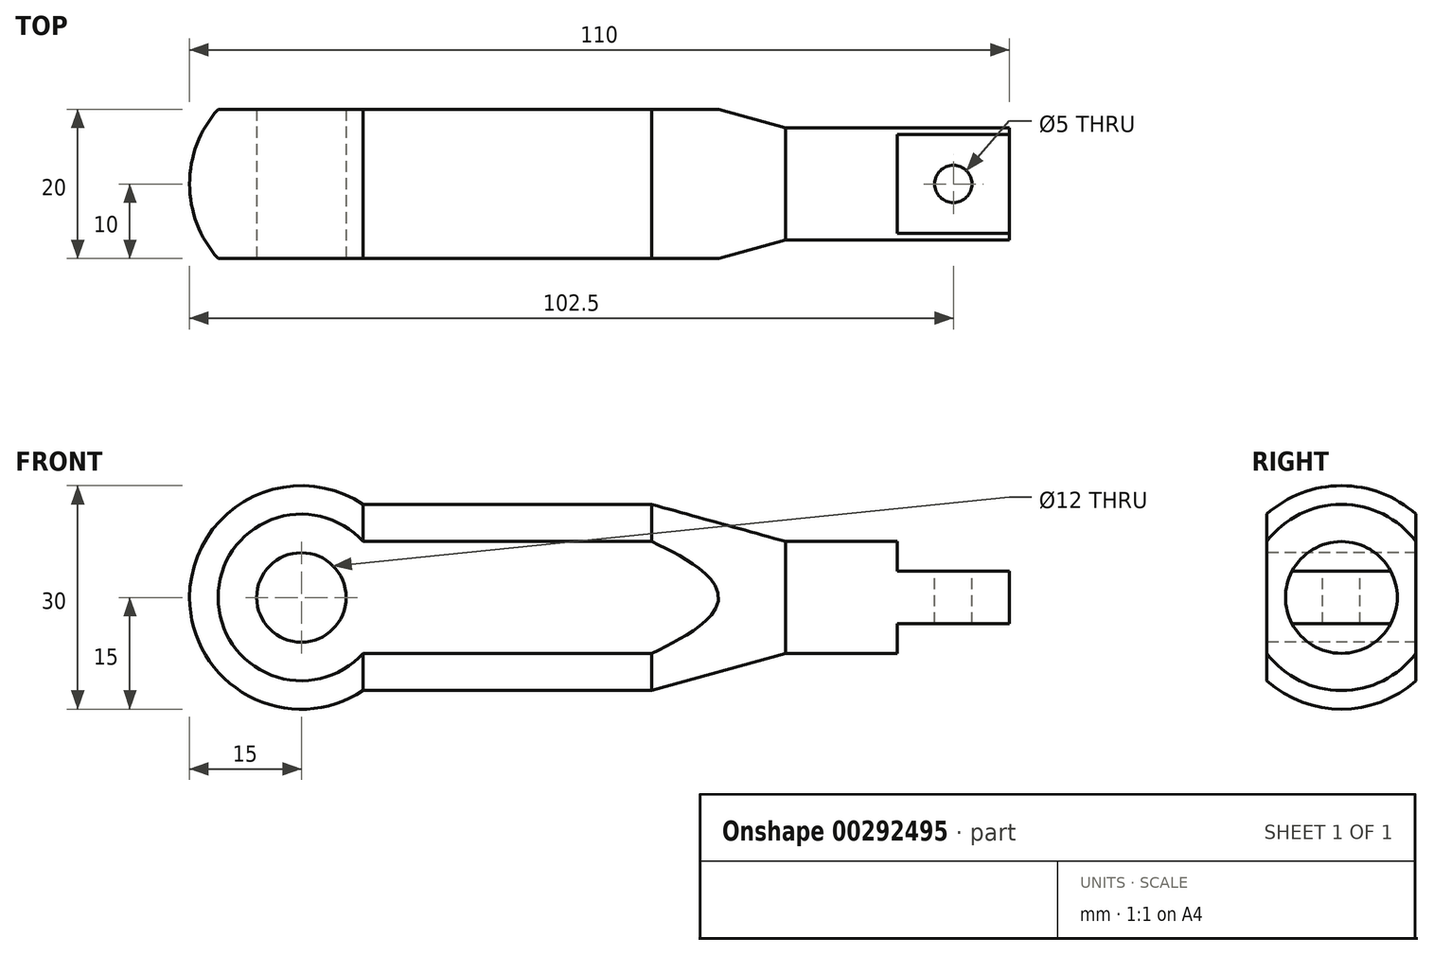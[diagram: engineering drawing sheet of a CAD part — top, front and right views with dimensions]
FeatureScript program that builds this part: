
annotation { "Feature Type Name" : "Feature", "Feature Type Description" : "" }
export const myFeature = defineFeature(function(context is Context, id is Id, definition is map)
    precondition{}
    {
        {
            var Q0;
            Q0=qCreatedBy(makeId("Front.planeOp"),FACE);
            var sketch = newSketch(context, id + "F0", { "sketchPlane" : qUnion([Q0])});
            skArc(sketch, "E0", {"start": v(15, 0) * mm, "mid": v(0, 15) * mm, "end": v(-15, 0) * mm});
            skLineSegment(sketch, "E1", {"start": v(0, 0) * mm, "end": v(95, 0) * mm});
            skLineSegment(sketch, "E2", {"start": v(95, 0) * mm, "end": v(95, 7.5) * mm});
            skLineSegment(sketch, "E3", {"start": v(95, 7.5) * mm, "end": v(47, 7.5) * mm});
            skLineSegment(sketch, "E4", {"start": v(47, 7.5) * mm, "end": v(47, 12.5) * mm});
            skLineSegment(sketch, "E5", {"start": v(47, 12.5) * mm, "end": v(8.3, 12.5) * mm});
            skLineSegment(sketch, "E6", {"start": v(47, 7.5) * mm, "end": v(65, 7.5) * mm});
            skLineSegment(sketch, "E7", {"start": v(65, 7.5) * mm, "end": v(47, 12.5) * mm});
            skLineSegment(sketch, "E8", {"start": v(0, 0) * mm, "end": v(-15, 0) * mm});
            skSolve(sketch);
        }
        {
            var Q0;
            {var subQ4=sQuery(id+"F0.wireOp",EDGE,"E8");Q0=makeQuery(id+"F0.imprint","IMPRINT",FACE,{"disambiguationData":[TD([[makeQuery(id+"F0.imprint","IMPRINT",EDGE,{"derivedFrom":subQ4}),-1.0]])]});}
            var Q1;
            {var subQ0=sQuery(id+"F0.wireOp",EDGE,"E2");Q1=makeQuery(id+"F0.imprint","IMPRINT",FACE,{"disambiguationData":[TD([[makeQuery(id+"F0.imprint","IMPRINT",EDGE,{"derivedFrom":subQ0}),1.0]])]});}
            var Q2;
            Q2=makeQuery(id+"F0.imprint","IMPRINT",FACE,{"disambiguationData":[TD([[makeQuery(id+"F0.imprint","IMPRINT",EDGE,{"derivedFrom":sQuery(id+"F0.wireOp",EDGE,"E4")}),-1.0]])]});
            var Q3;
            Q3=sQuery(id+"F0.wireOp",EDGE,"E1");
            revolve(context, id + "F1", {"entities" : qUnion([Q0, Q1, Q2]), "axis" : qUnion([Q3]), "revolveType" : RevolveType.FULL});
        }
        {
            var Q0;
            Q0=qCreatedBy(makeId("Top.planeOp"),FACE);
            var sketch = newSketch(context, id + "F2", { "sketchPlane" : qUnion([Q0])});
            skLineSegment(sketch, "E9", {"start": v(8.3, 12.5) * mm, "end": v(47, 12.5) * mm});
            skLineSegment(sketch, "E10", {"start": v(47, -12.5) * mm, "end": v(8.3, -12.5) * mm});
            skLineSegment(sketch, "E11", {"start": v(0, 0) * mm, "end": v(0, 10) * mm});
            skLineSegment(sketch, "E12", {"start": v(0, 10) * mm, "end": v(-19.78, 10) * mm});
            skLineSegment(sketch, "E13", {"start": v(-19.78, 10) * mm, "end": v(-19.78, -10) * mm});
            skLineSegment(sketch, "E14", {"start": v(-19.78, -10) * mm, "end": v(84.9, -10) * mm});
            skLineSegment(sketch, "E15", {"start": v(84.9, -10) * mm, "end": v(84.9, -25.16) * mm});
            skLineSegment(sketch, "E16", {"start": v(84.9, -25.16) * mm, "end": v(-32.5, -25.16) * mm});
            skLineSegment(sketch, "E17", {"start": v(-32.5, -25.16) * mm, "end": v(-32.5, 24) * mm});
            skLineSegment(sketch, "E18", {"start": v(0, 10) * mm, "end": v(81.8, 10) * mm});
            skLineSegment(sketch, "E19", {"start": v(81.8, 10) * mm, "end": v(81.8, 23.04) * mm});
            skLineSegment(sketch, "E20", {"start": v(81.8, 23.04) * mm, "end": v(-32.5, 24) * mm});
            skSolve(sketch);
        }
        {
            var Q0;
            Q0=makeQuery(id+"F2.imprint","IMPRINT",FACE,{"disambiguationData":[TD([[makeQuery(id+"F2.imprint","IMPRINT",EDGE,{"derivedFrom":sQuery(id+"F2.wireOp",EDGE,"E12")}),-1.0]])]});
            extrude(context, id + "F3", {"entities" : qUnion([Q0]), "operationType" : NewBodyOperationType.REMOVE, "endBound" : BoundingType.SYMMETRIC, "depth" : 40 * mm});
        }
        {
            var Q0;
            Q0=makeQuery(id+"F3.boolean.opBoolean","COPY",FACE,{"derivedFrom":makeQuery(id+"F3.opExtrude","SWEPT_FACE",FACE,{"disambiguationData":[OSD([sQuery(id+"F2.wireOp",EDGE,"E14")])]})});
            var sketch = newSketch(context, id + "F4", { "sketchPlane" : qUnion([Q0])});
            skCircle(sketch, "E21", {"center": v(0, 0) * mm, "radius": 6 * mm});
            skSolve(sketch);
        }
        {
            var Q0;
            Q0=makeQuery(id+"F4.imprint","IMPRINT",FACE,{"disambiguationData":[TD([[makeQuery(id+"F4.imprint","IMPRINT",EDGE,{"derivedFrom":sQuery(id+"F4.wireOp",EDGE,"E21")}),1.0]])]});
            extrude(context, id + "F5", {"entities" : qUnion([Q0]), "operationType" : NewBodyOperationType.REMOVE, "oppositeDirection" : true, "depth" : 25 * mm});
        }
        {
            var Q0;
            Q0=makeQuery(id+"F1.opRevolve","SWEPT_FACE",FACE,{"disambiguationData":[OSD([sQuery(id+"F0.wireOp",EDGE,"E2")])]});
            var sketch = newSketch(context, id + "F6", { "sketchPlane" : qUnion([Q0])});
            skLineSegment(sketch, "E22", {"start": v(-7.5, 0) * mm, "end": v(7.5, 0) * mm});
            skLineSegment(sketch, "E23.0", {"start": v(-7.5, -3.5) * mm, "end": v(7.5, -3.5) * mm});
            skLineSegment(sketch, "E24.0", {"start": v(-7.5, 3.5) * mm, "end": v(7.5, 3.5) * mm});
            skLineSegment(sketch, "E25", {"start": v(7.5, 3.5) * mm, "end": v(7.5, -3.5) * mm});
            skLineSegment(sketch, "E26", {"start": v(-7.5, 3.5) * mm, "end": v(-7.5, -3.5) * mm});
            skCircle(sketch, "E27.0.0", {"center": v(0, 0) * mm, "radius": 7.5 * mm});
            skSolve(sketch);
        }
        {
            var Q0;
            {var subQ0=sQuery(id+"F6.wireOp",EDGE,"E27.0.0");var subQ1=sQuery(id+"F6.wireOp",EDGE,"E24.0");var subQ2=makeQuery(id+"F6.imprint","INTERSECT",VERTEX,{"disambiguationData":[OD(0.0)],"derivedFrom":[subQ1,subQ0]});Q0=makeQuery(id+"F6.imprint","IMPRINT",FACE,{"disambiguationData":[TD([[makeQuery(id+"F6.imprint","IMPRINT",EDGE,{"disambiguationData":[TD([[subQ2,-1.0]])],"derivedFrom":subQ1}),1.0]])]});}
            var Q1;
            {var subQ0=sQuery(id+"F6.wireOp",EDGE,"E27.0.0");var subQ1=sQuery(id+"F6.wireOp",EDGE,"E23.0");var subQ2=makeQuery(id+"F6.imprint","INTERSECT",VERTEX,{"disambiguationData":[OD(0.0)],"derivedFrom":[subQ1,subQ0]});Q1=makeQuery(id+"F6.imprint","IMPRINT",FACE,{"disambiguationData":[TD([[makeQuery(id+"F6.imprint","IMPRINT",EDGE,{"disambiguationData":[TD([[subQ2,-1.0]])],"derivedFrom":subQ1}),-1.0]])]});}
            extrude(context, id + "F7", {"entities" : qUnion([Q0, Q1]), "operationType" : NewBodyOperationType.REMOVE, "oppositeDirection" : true, "depth" : 15 * mm});
        }
        {
            var Q0;
            Q0=makeQuery(id+"F7.boolean.opBoolean","COPY",FACE,{"derivedFrom":makeQuery(id+"F7.opExtrude","SWEPT_FACE",FACE,{"disambiguationData":[OSD([sQuery(id+"F6.wireOp",EDGE,"E24.0")])]})});
            var sketch = newSketch(context, id + "F8", { "sketchPlane" : qUnion([Q0])});
            skLineSegment(sketch, "E28", {"start": v(95, 0) * mm, "end": v(87.5, 0) * mm});
            skCircle(sketch, "E29", {"center": v(87.5, 0) * mm, "radius": 2.5 * mm});
            skSolve(sketch);
        }
        {
            var Q0;
            Q0=makeQuery(id+"F8.imprint","IMPRINT",FACE,{"disambiguationData":[TD([[makeQuery(id+"F8.imprint","IMPRINT",EDGE,{"derivedFrom":sQuery(id+"F8.wireOp",EDGE,"E29")}),1.0]])]});
            extrude(context, id + "F9", {"entities" : qUnion([Q0]), "operationType" : NewBodyOperationType.REMOVE, "oppositeDirection" : true, "depth" : 25 * mm});
        }
    });
